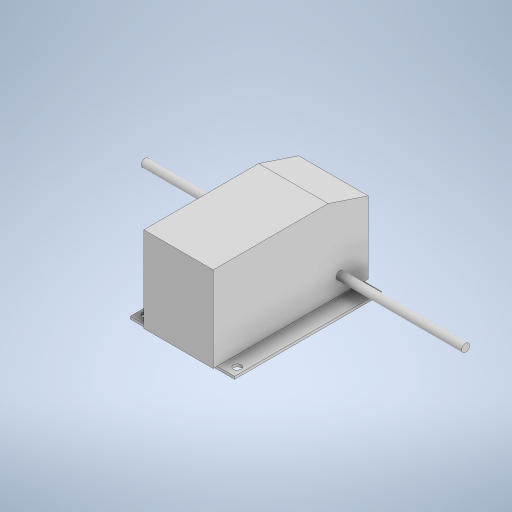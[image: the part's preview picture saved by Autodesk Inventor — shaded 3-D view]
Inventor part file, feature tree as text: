
AUTODESK INVENTOR PART (.ipt)
format: ipt  version: 2023.2 (Build 272271000, 271)  size: 315,392 bytes
history: native  units: mm
features: sketch x4
ambient origin geometry x8: Origin, YZ Plane, XZ Plane, XY Plane, X Axis, Y Axis, Z Axis, Center Point
bodies: Body1 (feature_tree)
feature tree (4):
  sketch  "Sketch1"  dims[d228=39.0mm]
  sketch  "Sketch2"  dims[d229=55.0mm]
  sketch  "Sketch3"  dims[d230=1.0mm d231=0.0mm]
  sketch  "Sketch4"  dims[d232=3.0mm d236=3.5mm d237=2.5mm d238=3.0mm d239=2.5mm d240=3.0mm d241=6.0mm d242=4.0mm d243=2.0mm d244=90.0deg d245=8.0mm d246=20.594885mm d249=32.0mm d250=0.0mm d251=15.0mm d252=5.0mm d253=45.0deg d257=26.0mm d258=58.0mm d259=6.5mm d260=1.5mm d272=3.0mm d273=10.5mm d274=6.5mm d275=120.0mm d276=0.0mm d9=0.5mm d10=0.872665mm d11=0.5mm d12=0.872665mm d13=0.5mm d14=0.872665mm d27=0.5mm d28=0.872665mm d29=0.5mm d30=0.872665mm d88=0.5mm d89=0.872665mm d90=0.5mm d91=0.872665mm d116=0.5mm d117=0.872665mm d118=0.5mm d119=0.872665mm d154=0.5mm d155=0.872665mm d156=0.5mm d157=0.872665mm d181=0.5mm d182=0.872665mm d183=0.5mm d184=0.872665mm d221=0.5mm d222=0.872665mm d223=0.5mm d224=0.872665mm d233=0.872665mm]
